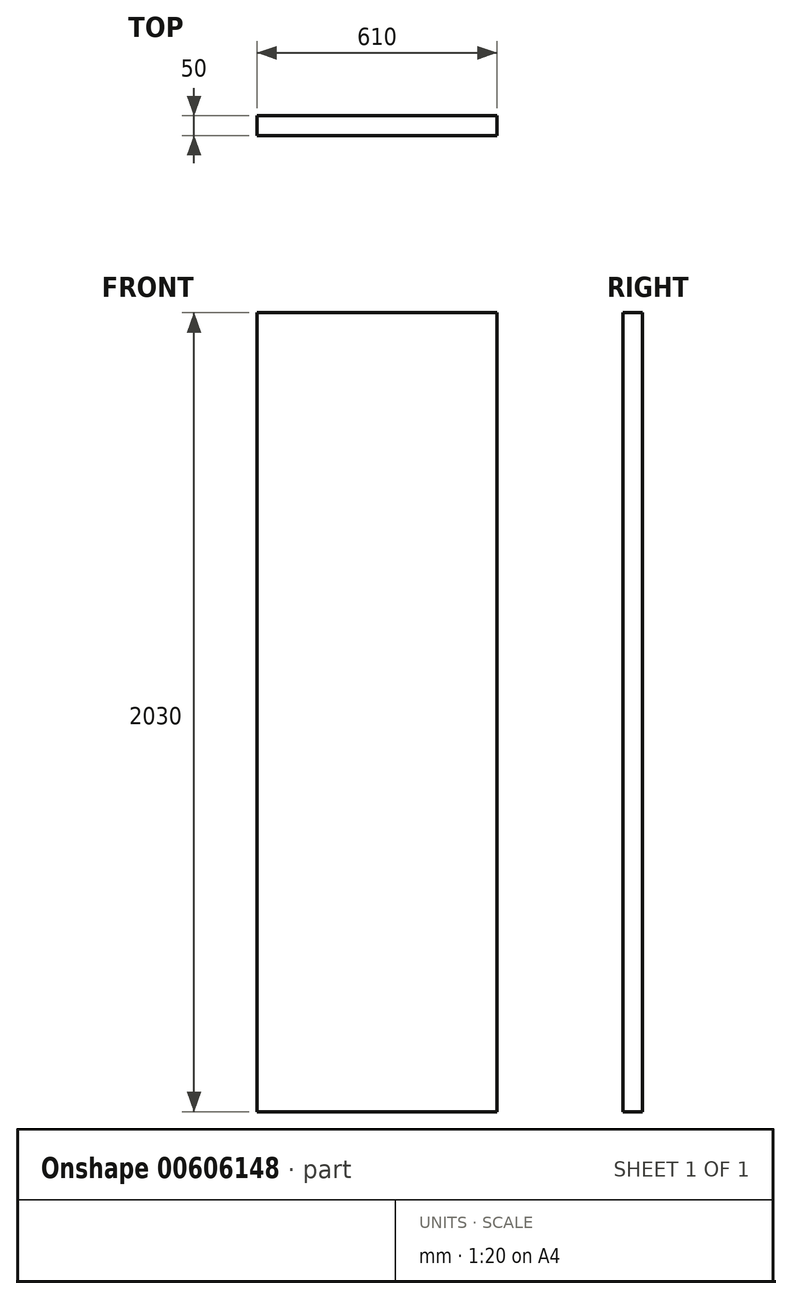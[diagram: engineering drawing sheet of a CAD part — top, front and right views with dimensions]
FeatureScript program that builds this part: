
annotation { "Feature Type Name" : "Feature", "Feature Type Description" : "" }
export const myFeature = defineFeature(function(context is Context, id is Id, definition is map)
    precondition{}
    {
        {
            var Q0;
            Q0=qCreatedBy(makeId("Front.planeOp"),FACE);
            var sketch = newSketch(context, id + "F0", { "sketchPlane" : qUnion([Q0])});
            skLineSegment(sketch, "E0.bottom", {"start": v(555.69, 1985.9) * mm, "end": v(-54.31, 1985.9) * mm});
            skLineSegment(sketch, "E0.top", {"start": v(555.69, -44.1) * mm, "end": v(-54.31, -44.1) * mm});
            skLineSegment(sketch, "E0.left", {"start": v(555.69, 1985.9) * mm, "end": v(555.69, -44.1) * mm});
            skLineSegment(sketch, "E0.right", {"start": v(-54.31, 1985.9) * mm, "end": v(-54.31, -44.1) * mm});
            skSolve(sketch);
        }
        {
            var Q0;
            Q0=qSketchRegion(id+"F0",true);
            extrude(context, id + "F1", {"entities" : qUnion([Q0]), "depth" : 50 * mm, "offsetDistance" : 25 * mm});
        }
    });
